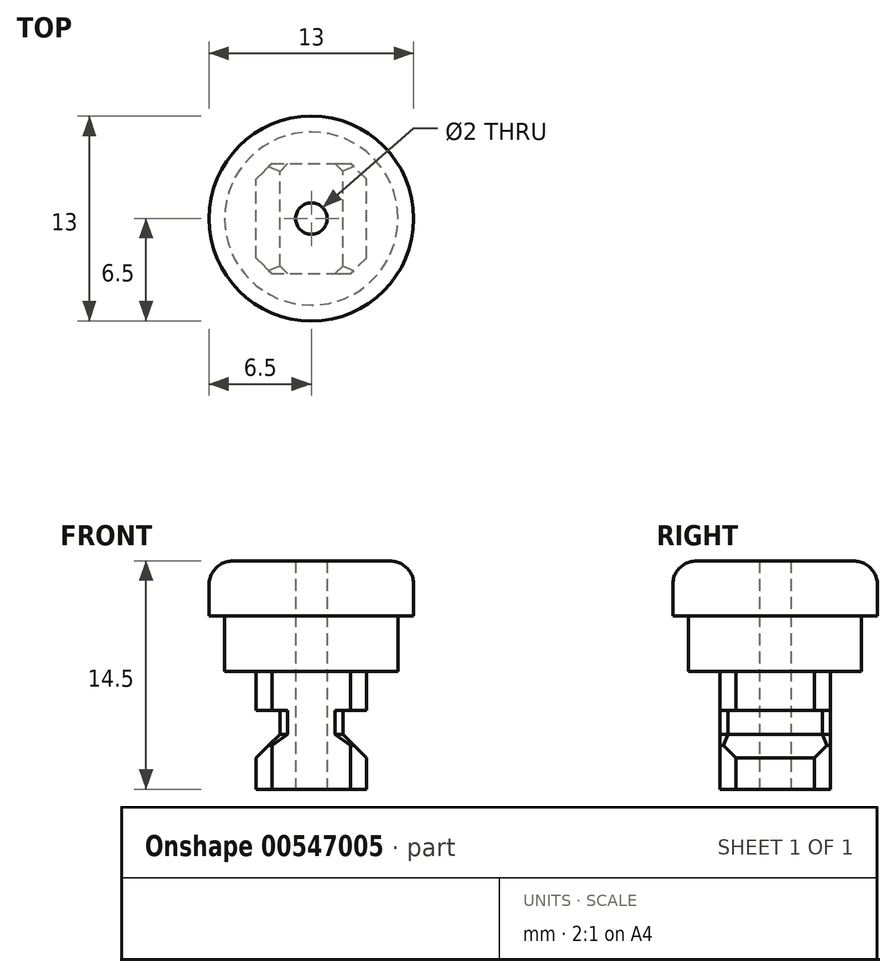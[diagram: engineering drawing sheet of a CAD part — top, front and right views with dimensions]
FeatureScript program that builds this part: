
annotation { "Feature Type Name" : "Feature", "Feature Type Description" : "" }
export const myFeature = defineFeature(function(context is Context, id is Id, definition is map)
    precondition{}
    {
        {
            var Q0;
            Q0=qCreatedBy(makeId("Front.planeOp"),FACE);
            var sketch = newSketch(context, id + "F0", { "sketchPlane" : qUnion([Q0])});
            skLineSegment(sketch, "E0", {"start": v(0, 0) * mm, "end": v(0, 7) * mm});
            skLineSegment(sketch, "E1", {"start": v(0, 7) * mm, "end": v(6.5, 7) * mm});
            skLineSegment(sketch, "E2", {"start": v(6.5, 7) * mm, "end": v(6.5, 3.5) * mm});
            skLineSegment(sketch, "E3", {"start": v(6.5, 3.5) * mm, "end": v(5.5, 3.5) * mm});
            skLineSegment(sketch, "E4", {"start": v(5.5, 3.5) * mm, "end": v(5.5, 0) * mm});
            skLineSegment(sketch, "E5", {"start": v(5.5, 0) * mm, "end": v(0, 0) * mm});
            skPoint(sketch, "E6.end.orphan", {"position": v(1, 0) * mm});
            skLineSegment(sketch, "E7", {"start": v(0, -2.89) * mm, "end": v(0, 12.94) * mm});
            skSolve(sketch);
        }
        {
            var Q0;
            {var subQ0=sQuery(id+"F0.wireOp",EDGE,"E1");Q0=makeQuery(id+"F0.imprint","IMPRINT",FACE,{"disambiguationData":[TD([[makeQuery(id+"F0.imprint","IMPRINT",EDGE,{"derivedFrom":subQ0}),-1.0]])]});}
            var Q1;
            Q1=sQuery(id+"F0.wireOp",EDGE,"E7");
            revolve(context, id + "F1", {"surfaceOperationType" : NewSurfaceOperationType.NEW, "entities" : qUnion([Q0]), "axis" : qUnion([Q1]), "revolveType" : RevolveType.FULL});
        }
        {
            var Q0;
            Q0=qCreatedBy(makeId("Front.planeOp"),FACE);
            var sketch = newSketch(context, id + "F2", { "sketchPlane" : qUnion([Q0])});
            skLineSegment(sketch, "E8.bottom", {"start": v(-3.5, 0) * mm, "end": v(3.5, 0) * mm});
            skLineSegment(sketch, "E8.top", {"start": v(-3.5, -7.5) * mm, "end": v(3.5, -7.5) * mm});
            skLineSegment(sketch, "E8.left", {"start": v(-3.5, 0) * mm, "end": v(-3.5, -2.5) * mm});
            skLineSegment(sketch, "E8.right", {"start": v(3.5, 0) * mm, "end": v(3.5, -2.5) * mm});
            skLineSegment(sketch, "E9", {"start": v(-3.5, -2.5) * mm, "end": v(-2, -2.5) * mm});
            skLineSegment(sketch, "E10", {"start": v(-3.5, -5.5) * mm, "end": v(-2, -5.5) * mm});
            skLineSegment(sketch, "E11", {"start": v(2, -2.5) * mm, "end": v(2, -5.5) * mm});
            skLineSegment(sketch, "E12", {"start": v(-2, -2.5) * mm, "end": v(-2, -5.5) * mm});
            skLineSegment(sketch, "E13.trimOffspring", {"start": v(-3.5, -5.5) * mm, "end": v(-3.5, -7.5) * mm});
            skLineSegment(sketch, "E14.trimOffspring", {"start": v(3.5, -5.5) * mm, "end": v(3.5, -7.5) * mm});
            skLineSegment(sketch, "E15.trimOffspring", {"start": v(2, -2.5) * mm, "end": v(3.5, -2.5) * mm});
            skLineSegment(sketch, "E16.trimOffspring", {"start": v(2, -5.5) * mm, "end": v(3.5, -5.5) * mm});
            skSolve(sketch);
        }
        {
            var Q0;
            Q0=makeQuery(id+"F2.imprint","IMPRINT",FACE,{"disambiguationData":[TD([[makeQuery(id+"F2.imprint","IMPRINT",EDGE,{"derivedFrom":sQuery(id+"F2.wireOp",EDGE,"E8.bottom")}),-1.0]])]});
            extrude(context, id + "F3", {"entities" : qUnion([Q0]), "operationType" : NewBodyOperationType.ADD, "depth" : 7 * mm, "offsetDistance" : 25 * mm, "symmetric" : true});
        }
        {
            var Q0;
            Q0=makeQuery(id+"F3.opExtrude","CAP_EDGE",EDGE,{"disambiguationData":[OSD([sQuery(id+"F2.wireOp",EDGE,"E8.right")])],"isStart":false});
            var Q1;
            Q1=makeQuery(id+"F3.opExtrude","CAP_EDGE",EDGE,{"disambiguationData":[OSD([sQuery(id+"F2.wireOp",EDGE,"E8.right")])],"isStart":true});
            var Q2;
            Q2=makeQuery(id+"F3.opExtrude","CAP_EDGE",EDGE,{"disambiguationData":[OSD([sQuery(id+"F2.wireOp",EDGE,"E8.left")])],"isStart":true});
            var Q3;
            Q3=makeQuery(id+"F3.opExtrude","CAP_EDGE",EDGE,{"disambiguationData":[OSD([sQuery(id+"F2.wireOp",EDGE,"E8.left")])],"isStart":false});
            var Q4;
            Q4=makeQuery(id+"F3.opExtrude","CAP_EDGE",EDGE,{"disambiguationData":[OSD([sQuery(id+"F2.wireOp",EDGE,"E13.trimOffspring")])],"isStart":false});
            var Q5;
            Q5=makeQuery(id+"F3.opExtrude","CAP_EDGE",EDGE,{"disambiguationData":[OSD([sQuery(id+"F2.wireOp",EDGE,"E14.trimOffspring")])],"isStart":false});
            var Q6;
            Q6=makeQuery(id+"F3.opExtrude","CAP_EDGE",EDGE,{"disambiguationData":[OSD([sQuery(id+"F2.wireOp",EDGE,"E13.trimOffspring")])],"isStart":true});
            var Q7;
            Q7=makeQuery(id+"F3.opExtrude","CAP_EDGE",EDGE,{"disambiguationData":[OSD([sQuery(id+"F2.wireOp",EDGE,"E14.trimOffspring")])],"isStart":true});
            chamfer(context, id + "F4", {"entities" : qUnion([Q0, Q1, Q2, Q3, Q4, Q5, Q6, Q7]), "width" : 1 * mm, "tangentPropagation" : true});
        }
        {
            var Q0;
            Q0=makeQuery(id+"F3.opExtrude","CAP_EDGE",EDGE,{"disambiguationData":[OSD([sQuery(id+"F2.wireOp",EDGE,"E11")])],"isStart":false});
            var Q1;
            Q1=makeQuery(id+"F3.opExtrude","CAP_EDGE",EDGE,{"disambiguationData":[OSD([sQuery(id+"F2.wireOp",EDGE,"E12")])],"isStart":false});
            var Q2;
            Q2=makeQuery(id+"F3.opExtrude","CAP_EDGE",EDGE,{"disambiguationData":[OSD([sQuery(id+"F2.wireOp",EDGE,"E12")])],"isStart":true});
            var Q3;
            Q3=makeQuery(id+"F3.opExtrude","CAP_EDGE",EDGE,{"disambiguationData":[OSD([sQuery(id+"F2.wireOp",EDGE,"E11")])],"isStart":true});
            chamfer(context, id + "F5", {"entities" : qUnion([Q0, Q1, Q2, Q3]), "width" : 0.5 * mm, "tangentPropagation" : true});
        }
        {
            var Q0;
            Q0=makeQuery(id+"F5.opChamfer","BLEND_EDGE",EDGE,{"blendedFrom":[makeQuery(id+"F3.opExtrude","CAP_EDGE",EDGE,{"disambiguationData":[OSD([sQuery(id+"F2.wireOp",EDGE,"E12")])],"isStart":false}),makeQuery(id+"F3.opExtrude","SWEPT_FACE",FACE,{"disambiguationData":[OSD([sQuery(id+"F2.wireOp",EDGE,"E10")])]})],"blendedInto":[makeQuery(id+"F3.opExtrude","SWEPT_FACE",FACE,{"disambiguationData":[OSD([sQuery(id+"F2.wireOp",EDGE,"E10")])]})]});
            var Q1;
            Q1=makeQuery(id+"F3.opExtrude","SWEPT_EDGE",EDGE,{"disambiguationData":[OSD([sQuery(id+"F2.wireOp",EDGE,"E10"),sQuery(id+"F2.wireOp",EDGE,"E12")])]});
            var Q2;
            Q2=makeQuery(id+"F5.opChamfer","BLEND_EDGE",EDGE,{"blendedFrom":[makeQuery(id+"F3.opExtrude","CAP_EDGE",EDGE,{"disambiguationData":[OSD([sQuery(id+"F2.wireOp",EDGE,"E12")])],"isStart":true}),makeQuery(id+"F3.opExtrude","SWEPT_FACE",FACE,{"disambiguationData":[OSD([sQuery(id+"F2.wireOp",EDGE,"E10")])]})],"blendedInto":[makeQuery(id+"F3.opExtrude","SWEPT_FACE",FACE,{"disambiguationData":[OSD([sQuery(id+"F2.wireOp",EDGE,"E10")])]})]});
            var Q3;
            Q3=makeQuery(id+"F5.opChamfer","BLEND_EDGE",EDGE,{"blendedFrom":[makeQuery(id+"F3.opExtrude","CAP_EDGE",EDGE,{"disambiguationData":[OSD([sQuery(id+"F2.wireOp",EDGE,"E11")])],"isStart":false}),makeQuery(id+"F3.opExtrude","SWEPT_FACE",FACE,{"disambiguationData":[OSD([sQuery(id+"F2.wireOp",EDGE,"E16.trimOffspring")])]})],"blendedInto":[makeQuery(id+"F3.opExtrude","SWEPT_FACE",FACE,{"disambiguationData":[OSD([sQuery(id+"F2.wireOp",EDGE,"E16.trimOffspring")])]})]});
            var Q4;
            Q4=makeQuery(id+"F3.opExtrude","SWEPT_EDGE",EDGE,{"disambiguationData":[OSD([sQuery(id+"F2.wireOp",EDGE,"E11"),sQuery(id+"F2.wireOp",EDGE,"E16.trimOffspring")])]});
            var Q5;
            Q5=makeQuery(id+"F5.opChamfer","BLEND_EDGE",EDGE,{"blendedFrom":[makeQuery(id+"F3.opExtrude","CAP_EDGE",EDGE,{"disambiguationData":[OSD([sQuery(id+"F2.wireOp",EDGE,"E11")])],"isStart":true}),makeQuery(id+"F3.opExtrude","SWEPT_FACE",FACE,{"disambiguationData":[OSD([sQuery(id+"F2.wireOp",EDGE,"E16.trimOffspring")])]})],"blendedInto":[makeQuery(id+"F3.opExtrude","SWEPT_FACE",FACE,{"disambiguationData":[OSD([sQuery(id+"F2.wireOp",EDGE,"E16.trimOffspring")])]})]});
            chamfer(context, id + "F6", {"entities" : qUnion([Q0, Q1, Q2, Q3, Q4, Q5]), "width" : 1.5 * mm, "tangentPropagation" : true});
        }
        {
            var Q0;
            Q0=makeQuery(id+"F1.opRevolve","SWEPT_EDGE",EDGE,{"disambiguationData":[OSD([sQuery(id+"F0.wireOp",EDGE,"E1"),sQuery(id+"F0.wireOp",EDGE,"E2")])]});
            fillet(context, id + "F7", {"entities" : qUnion([Q0]), "radius" : 1.5 * mm, "tangentPropagation" : true, "allowEdgeOverflow" : false});
        }
        {
            var Q0;
            Q0=makeQuery(id+"F3.opExtrude","SWEPT_FACE",FACE,{"disambiguationData":[OSD([sQuery(id+"F2.wireOp",EDGE,"E8.top")])]});
            var sketch = newSketch(context, id + "F8", { "sketchPlane" : qUnion([Q0])});
            skCircle(sketch, "E17", {"center": v(0, 0) * mm, "radius": 1 * mm});
            skSolve(sketch);
        }
        {
            var Q0;
            Q0=makeQuery(id+"F8.imprint","IMPRINT",FACE,{"disambiguationData":[TD([[makeQuery(id+"F8.imprint","IMPRINT",EDGE,{"derivedFrom":sQuery(id+"F8.wireOp",EDGE,"E17")}),1.0]])]});
            extrude(context, id + "F9", {"entities" : qUnion([Q0]), "operationType" : NewBodyOperationType.REMOVE, "oppositeDirection" : true, "depth" : 25 * mm, "offsetDistance" : 25 * mm});
        }
    });
